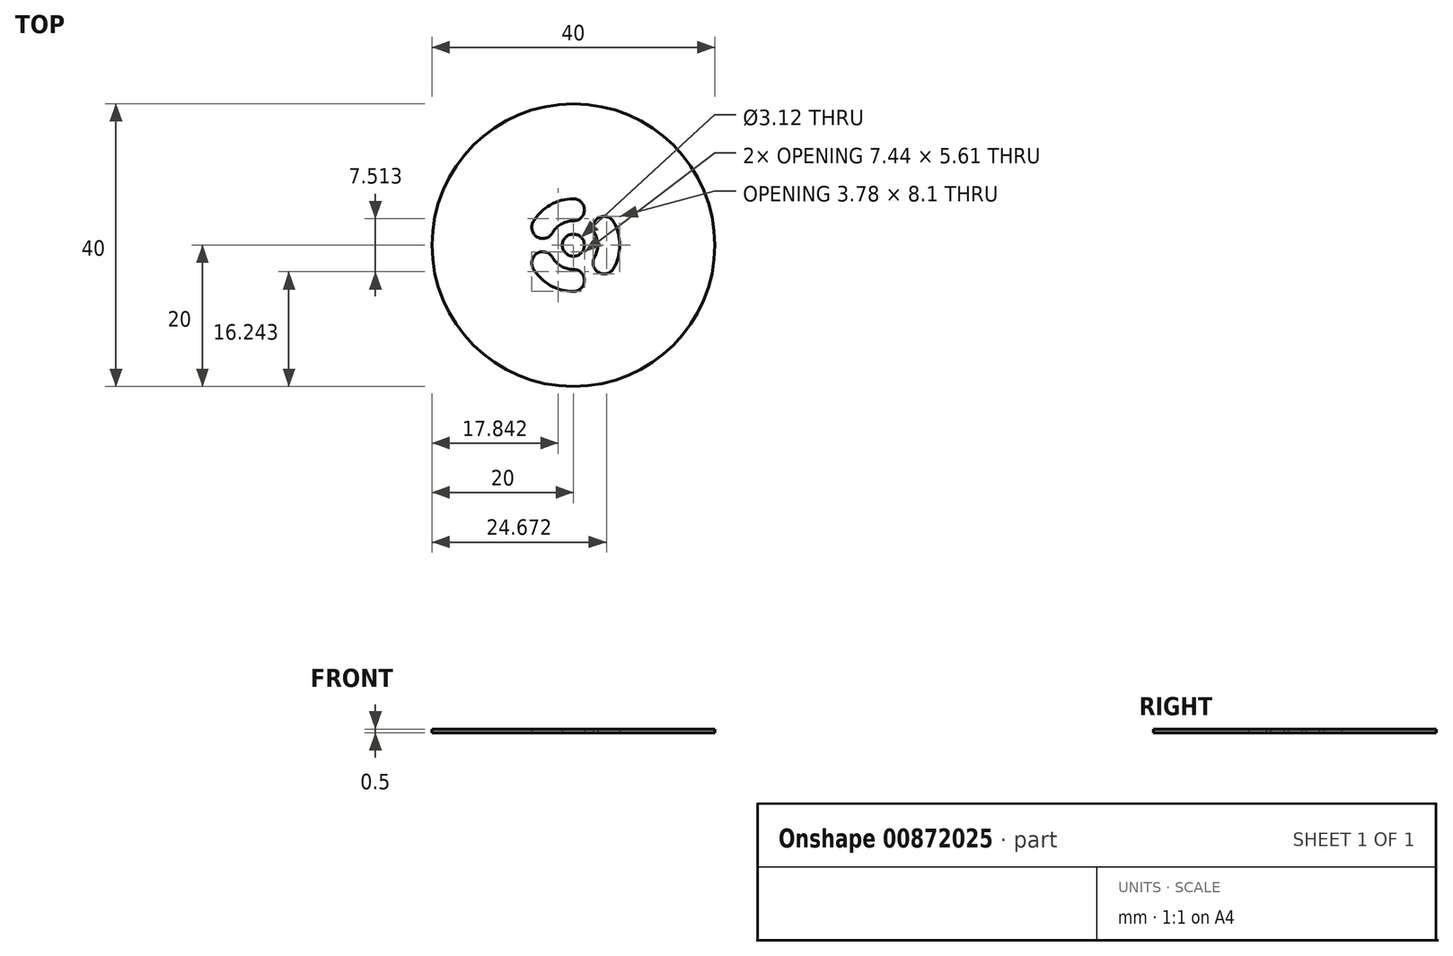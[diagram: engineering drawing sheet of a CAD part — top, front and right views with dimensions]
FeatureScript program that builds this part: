
annotation { "Feature Type Name" : "Feature", "Feature Type Description" : "" }
export const myFeature = defineFeature(function(context is Context, id is Id, definition is map)
    precondition{}
    {
        {
            var Q0;
            Q0=qCreatedBy(makeId("Top.planeOp"),FACE);
            var sketch = newSketch(context, id + "F0", { "sketchPlane" : qUnion([Q0])});
            skCircle(sketch, "E0", {"center": v(0, 0) * mm, "radius": 20 * mm});
            skCircle(sketch, "E1", {"center": v(0, 0) * mm, "radius": 1.56 * mm});
            skArc(sketch, "E2", {"start": v(0, 3.44) * mm, "mid": v(1.56, 5) * mm, "end": v(0, 6.56) * mm});
            skArc(sketch, "E3.1.0", {"start": v(-5.68, 3.28) * mm, "mid": v(-5.11, 1.15) * mm, "end": v(-2.98, 1.72) * mm});
            skArc(sketch, "E3.2.0", {"start": v(-2.98, -1.72) * mm, "mid": v(-5.11, -1.15) * mm, "end": v(-5.68, -3.28) * mm});
            skArc(sketch, "E3.3.0", {"start": v(0, -6.56) * mm, "mid": v(1.56, -5) * mm, "end": v(0, -3.44) * mm});
            skArc(sketch, "E3.4.0", {"start": v(2.98, -1.72) * mm, "mid": v(3.55, -3.85) * mm, "end": v(5.68, -3.28) * mm});
            skArc(sketch, "E3.5.0", {"start": v(5.68, 3.28) * mm, "mid": v(3.55, 3.85) * mm, "end": v(2.98, 1.72) * mm});
            skArc(sketch, "E4", {"start": v(0, 3.44) * mm, "mid": v(-1.72, 2.98) * mm, "end": v(-2.98, 1.72) * mm});
            skArc(sketch, "E5", {"start": v(0, 6.56) * mm, "mid": v(-3.28, 5.68) * mm, "end": v(-5.68, 3.28) * mm});
            skArc(sketch, "E6.trimOffspring", {"start": v(-2.98, -1.72) * mm, "mid": v(-1.72, -2.98) * mm, "end": v(0, -3.44) * mm});
            skArc(sketch, "E7.trimOffspring", {"start": v(-5.68, -3.28) * mm, "mid": v(-3.28, -5.68) * mm, "end": v(0, -6.56) * mm});
            skArc(sketch, "E8.trimOffspring", {"start": v(2.98, -1.72) * mm, "mid": v(3.44, 0) * mm, "end": v(2.98, 1.72) * mm});
            skArc(sketch, "E9.trimOffspring", {"start": v(5.68, -3.28) * mm, "mid": v(6.56, 0) * mm, "end": v(5.68, 3.28) * mm});
            skSolve(sketch);
        }
        {
            var Q0;
            Q0=makeQuery(id+"F0.imprint","IMPRINT",FACE,{"disambiguationData":[TD([[makeQuery(id+"F0.imprint","IMPRINT",EDGE,{"derivedFrom":sQuery(id+"F0.wireOp",EDGE,"E0")}),1.0]])]});
            extrude(context, id + "F1", {"entities" : qUnion([Q0]), "depth" : .5 * mm, "offsetDistance" : 25 * mm});
        }
    });
